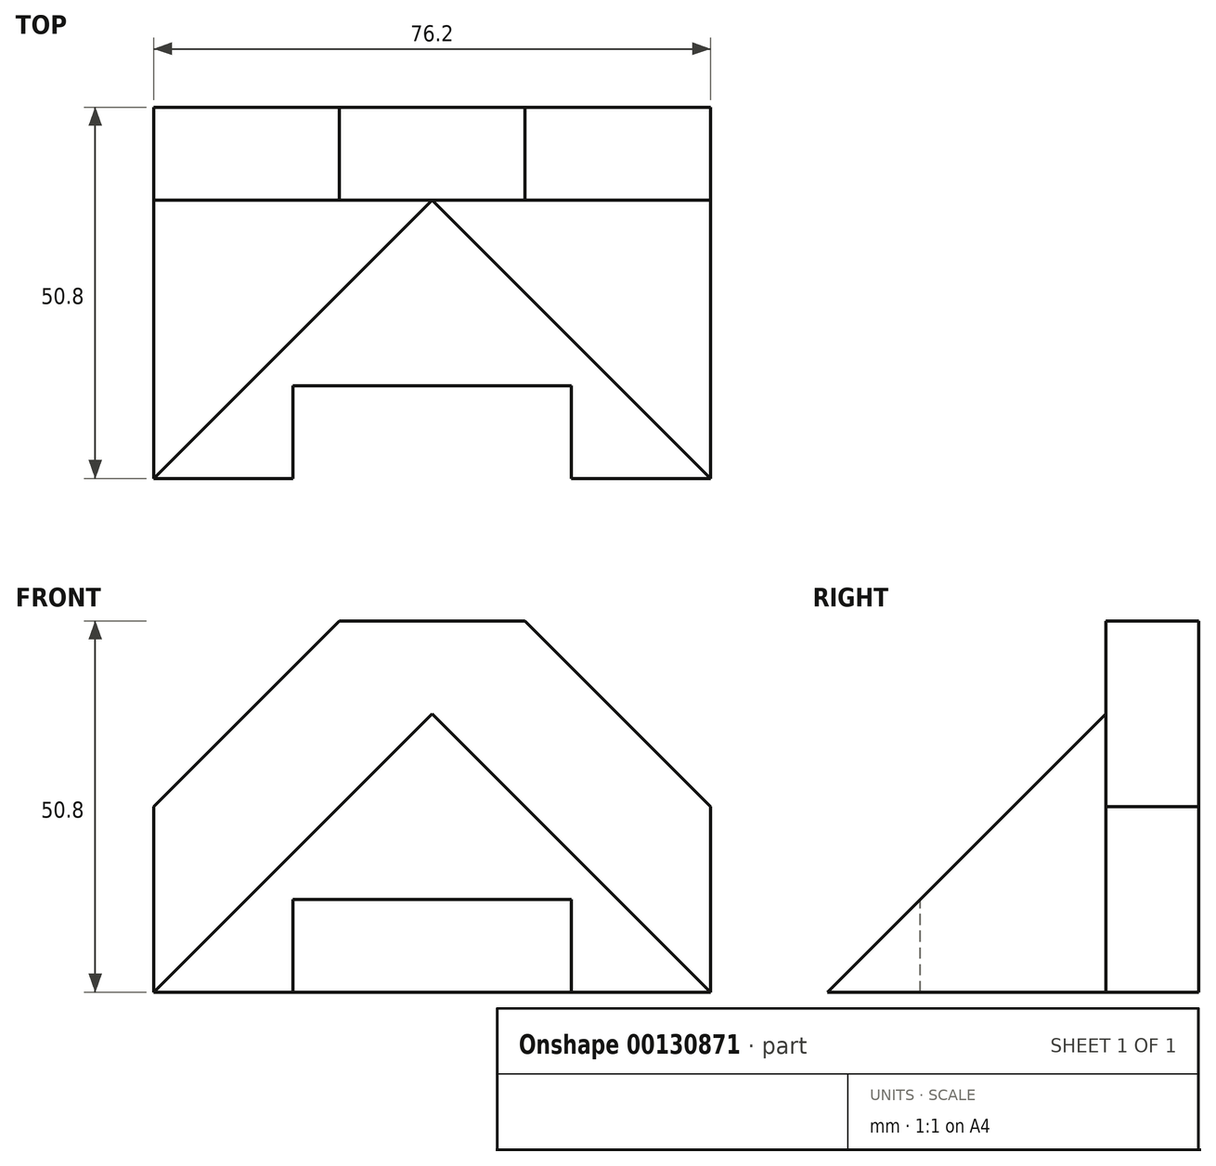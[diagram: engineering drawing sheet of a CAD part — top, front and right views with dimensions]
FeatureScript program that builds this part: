
annotation { "Feature Type Name" : "Feature", "Feature Type Description" : "" }
export const myFeature = defineFeature(function(context is Context, id is Id, definition is map)
    precondition{}
    {
        {
            var Q0;
            Q0=qCreatedBy(makeId("Top.planeOp"),FACE);
            var sketch = newSketch(context, id + "F0", { "sketchPlane" : qUnion([Q0])});
            skLineSegment(sketch, "E0.bottom", {"start": v(-38.1, 0) * mm, "end": v(38.1, 0) * mm});
            skLineSegment(sketch, "E0.top", {"start": v(-38.1, 50.8) * mm, "end": v(38.1, 50.8) * mm});
            skLineSegment(sketch, "E0.left", {"start": v(-38.1, 0) * mm, "end": v(-38.1, 50.8) * mm});
            skLineSegment(sketch, "E0.right", {"start": v(38.1, 0) * mm, "end": v(38.1, 50.8) * mm});
            skSolve(sketch);
        }
        {
            var Q0;
            Q0 = qSketchRegion(id + "F0", true);
            extrude(context, id + "F1", {"entities" : qUnion([Q0]), "oppositeDirection" : true, "depth" : 50.8 * mm});
        }
        {
            var Q0;
            Q0=qCreatedBy(makeId("Top.planeOp"),FACE);
            var sketch = newSketch(context, id + "F2", { "sketchPlane" : qUnion([Q0])});
            skLineSegment(sketch, "E1.bottom", {"start": v(-19.05, 0) * mm, "end": v(19.05, 0) * mm});
            skLineSegment(sketch, "E1.top", {"start": v(-19.05, 12.7) * mm, "end": v(19.05, 12.7) * mm});
            skLineSegment(sketch, "E1.left", {"start": v(-19.05, 0) * mm, "end": v(-19.05, 12.7) * mm});
            skLineSegment(sketch, "E1.right", {"start": v(19.05, 0) * mm, "end": v(19.05, 12.7) * mm});
            skSolve(sketch);
        }
        {
            var Q0;
            Q0 = qSketchRegion(id + "F2", true);
            extrude(context, id + "F3", {"entities" : qUnion([Q0]), "operationType" : NewBodyOperationType.REMOVE, "endBound" : BoundingType.THROUGH_ALL, "oppositeDirection" : true, "depth" : 25.4 * mm});
        }
        {
            var Q0;
            Q0=qCreatedBy(makeId("Right.planeOp"),FACE);
            var sketch = newSketch(context, id + "F4", { "sketchPlane" : qUnion([Q0])});
            skLineSegment(sketch, "E2", {"start": v(38.1, -12.7) * mm, "end": v(0, -50.8) * mm});
            skLineSegment(sketch, "E3", {"start": v(38.1, -12.7) * mm, "end": v(38.1, 0) * mm});
            skLineSegment(sketch, "E4", {"start": v(38.1, 0) * mm, "end": v(0, 0) * mm});
            skLineSegment(sketch, "E5", {"start": v(0, 0) * mm, "end": v(0, -50.8) * mm});
            skSolve(sketch);
        }
        {
            var Q0;
            Q0 = qSketchRegion(id + "F4", true);
            extrude(context, id + "F5", {"entities" : qUnion([Q0]), "operationType" : NewBodyOperationType.REMOVE, "endBound" : BoundingType.THROUGH_ALL, "oppositeDirection" : true, "depth" : 25.4 * mm, "hasSecondDirection" : true, "secondDirectionBound" : SecondDirectionBoundingType.THROUGH_ALL, "secondDirectionOppositeDirection" : false, "secondDirectionDepth" : 25.4 * mm});
        }
        {
            var Q0;
            Q0=qCreatedBy(makeId("Front.planeOp"),FACE);
            var sketch = newSketch(context, id + "F6", { "sketchPlane" : qUnion([Q0])});
            skLineSegment(sketch, "E6", {"start": v(12.7, 0) * mm, "end": v(38.1, -25.4) * mm});
            skLineSegment(sketch, "E7", {"start": v(38.1, -25.4) * mm, "end": v(38.1, 0) * mm});
            skLineSegment(sketch, "E8", {"start": v(38.1, 0) * mm, "end": v(12.7, 0) * mm});
            skLineSegment(sketch, "E9", {"start": v(-38.1, 0) * mm, "end": v(-38.1, -25.4) * mm});
            skLineSegment(sketch, "E10", {"start": v(-38.1, -25.4) * mm, "end": v(-12.7, 0) * mm});
            skLineSegment(sketch, "E11", {"start": v(-12.7, 0) * mm, "end": v(-38.1, 0) * mm});
            skSolve(sketch);
        }
        {
            var Q0;
            Q0 = qSketchRegion(id + "F6", true);
            extrude(context, id + "F7", {"entities" : qUnion([Q0]), "operationType" : NewBodyOperationType.REMOVE, "endBound" : BoundingType.THROUGH_ALL, "oppositeDirection" : true, "depth" : 25.4 * mm});
        }
        {
            var Q0;
            Q0=qCreatedBy(makeId("Front.planeOp"),FACE);
            var sketch = newSketch(context, id + "F8", { "sketchPlane" : qUnion([Q0])});
            skLineSegment(sketch, "E12", {"start": v(-38.1, -50.8) * mm, "end": v(0, -12.7) * mm});
            skLineSegment(sketch, "E13", {"start": v(0, -12.7) * mm, "end": v(38.1, -50.8) * mm});
            skLineSegment(sketch, "E14", {"start": v(38.1, -50.8) * mm, "end": v(38.1, -12.7) * mm});
            skLineSegment(sketch, "E15", {"start": v(38.1, -12.7) * mm, "end": v(-38.1, -12.7) * mm});
            skLineSegment(sketch, "E16", {"start": v(-38.1, -12.7) * mm, "end": v(-38.1, -50.8) * mm});
            skSolve(sketch);
        }
        {
            var Q0;
            Q0 = qSketchRegion(id + "F8", true);
            extrude(context, id + "F9", {"entities" : qUnion([Q0]), "operationType" : NewBodyOperationType.REMOVE, "oppositeDirection" : true, "depth" : 38.1 * mm});
        }
    });
